FCSTD DOCUMENT  (FreeCAD 0.18R16146 (Git))
Label: anse
License: All rights reserved
LicenseURL: http://en.wikipedia.org/wiki/All_rights_reserved
objects: Sketcher::SketchObject×1, PartDesign::Body×1
note: 2 computed .brp shape members not serialized (recipe doc carries the construction recipe); baked Part::Feature solids carry a one-line shape summary decoded from their .brp

FEATURE [Sketcher::SketchObject] Sketch
  MapMode = 5
  Support = -> [XY_Plane]
  sketch-geometry (3):
    g0: LineSegment StartX=0 StartY=0 StartZ=0 EndX=15 EndY=0 EndZ=0
    g1: LineSegment StartX=15 StartY=0 StartZ=0 EndX=15 EndY=20 EndZ=0
    g2: LineSegment StartX=6.93262 StartY=20 StartZ=0 EndX=15 EndY=20 EndZ=0
  constraints (9):
    c: PointOnObject(g0,g-2)
    c: PointOnObject(g0,g-1)
    c: PointOnObject(g0,g-1)
    c: Coincident(g1,g0)
    c: Vertical(g1)
    c: Horizontal(g2)
    c: Coincident(g2,g1)
    c: DistanceX(g0,g0) = 15
    c: DistanceY(g1,g1) = 20
FEATURE [PartDesign::Body] Body
  Group = -> [Sketch]
  Origin = -> Origin
